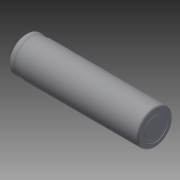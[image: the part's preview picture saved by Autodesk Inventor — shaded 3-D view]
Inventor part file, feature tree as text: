
AUTODESK INVENTOR PART (.ipt)
format: ipt  version: 2014 (Build 180170000, 170)  size: 153,600 bytes
history: native  units: mm
features: fillet x4, sketch x4, extrude x3, revolve x1, plane x1, mirror x1
ambient origin geometry x8: Origin, YZ Plane, XZ Plane, XY Plane, X Axis, Y Axis, Z Axis, Center Point
bodies: Volumenkörper1 (feature_tree)
feature tree (14):
  revolve  "Umdrehung1"
  plane  "Arbeitsebene1"
  fillet  "Rundung1"  Radius=67.0mm
  fillet  "Rundung2"  Radius=9.1mm
  extrude  "Extrusion1"  Depth=3.0mm
  mirror  "Spiegeln1"
  extrude  "Extrusion2"  TaperAngle=90.0deg  [1 undecoded]
  fillet  "Rundung3"  Radius=2.0mm
  extrude  "Extrusion3"  Depth=0.2mm
  fillet  "Rundung4"  Radius=0.2mm
  sketch  "Skizze1"  dims[d2=3.0mm d3=3.0mm]
  sketch  "Skizze2"  dims[d4=0.35mm d5=90.0deg d6=2.0mm]
  sketch  "Skizze3"  dims[d7=1.0mm d8=13.0mm d9=0.2mm d10=0.0mm]
  sketch  "Skizze4"  dims[d11=5.7mm d12=1.0mm d13=0.0mm d14=0.5mm d15=1.0mm d16=0.2mm d17=0.0mm d18=0.5mm]
note: 1 required parameter value undecoded (feature->parameter linkage not recoverable at this tier; creation-order binding heuristic only, values carry confidence <= 0.55)
